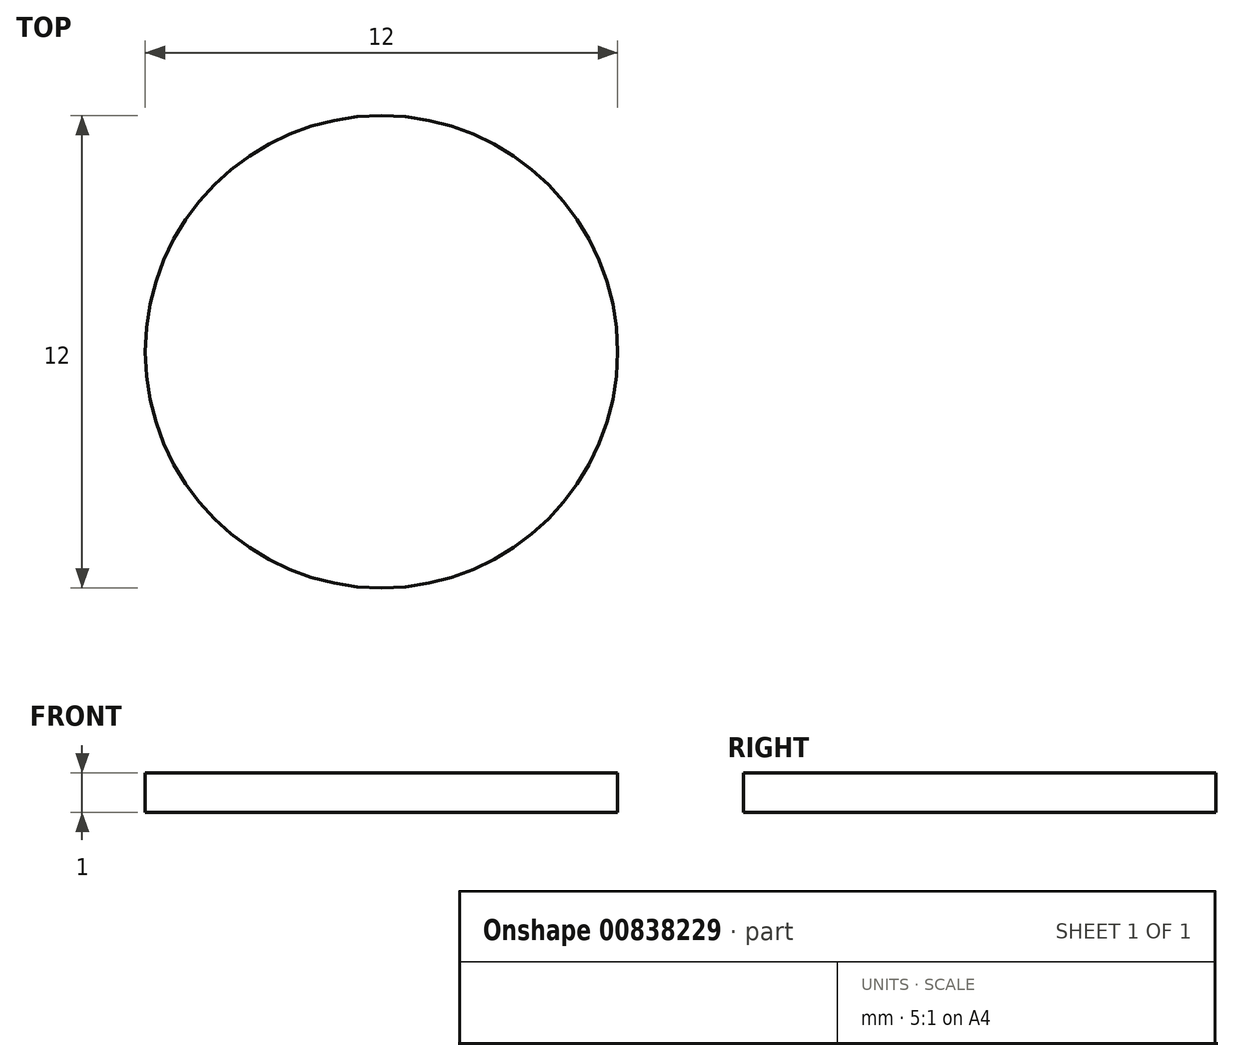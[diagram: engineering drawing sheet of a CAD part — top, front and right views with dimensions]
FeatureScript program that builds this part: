
annotation { "Feature Type Name" : "Feature", "Feature Type Description" : "" }
export const myFeature = defineFeature(function(context is Context, id is Id, definition is map)
    precondition{}
    {
        {
            var Q0;
            Q0=qCreatedBy(makeId("Top.planeOp"),FACE);
            var sketch = newSketch(context, id + "F0", { "sketchPlane" : qUnion([Q0])});
            skCircle(sketch, "E0", {"center": v(0, 0) * mm, "radius": 6 * mm});
            skSolve(sketch);
        }
        {
            var Q0;
            Q0=makeQuery(id+"F0.imprint","IMPRINT",FACE,{"disambiguationData":[TD([[makeQuery(id+"F0.imprint","IMPRINT",EDGE,{"derivedFrom":sQuery(id+"F0.wireOp",EDGE,"E0")}),1.0]])]});
            extrude(context, id + "F1", {"entities" : qUnion([Q0]), "depth" : 1 * mm, "offsetDistance" : 25 * mm});
        }
    });
